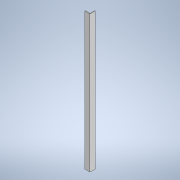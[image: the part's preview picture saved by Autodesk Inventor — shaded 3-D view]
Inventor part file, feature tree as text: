
AUTODESK INVENTOR PART (.ipt)
format: ipt  version: 2022 (Build 260153000, 153)  size: 98,304 bytes
history: native  units: mm
features: extrude x1, sketch x1
ambient origin geometry x8: Origin, YZ Plane, XZ Plane, XY Plane, X Axis, Y Axis, Z Axis, Center Point
bodies: Solid1 (feature_tree)
feature tree (2):
  extrude  "Extrusion1"  Depth=50.0mm
  sketch  "Sketch1"  dims[d0=50.0mm d1=50.0mm d2=5.0mm d3=5.0mm d4=1300.0mm d5=0.0mm]
